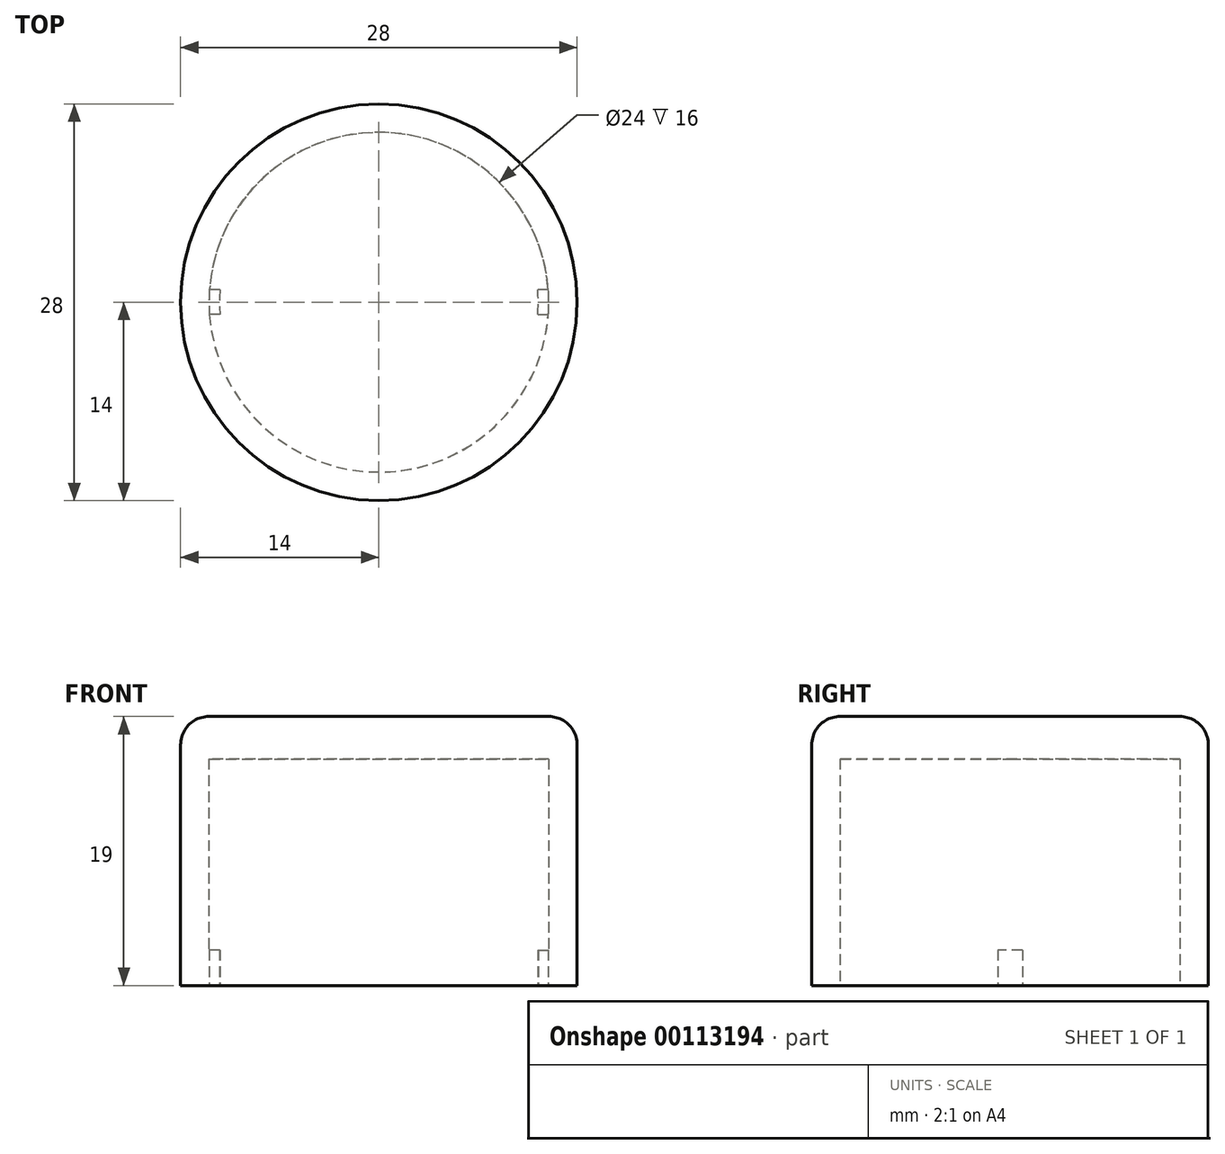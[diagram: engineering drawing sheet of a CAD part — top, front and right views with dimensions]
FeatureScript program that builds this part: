
annotation { "Feature Type Name" : "Feature", "Feature Type Description" : "" }
export const myFeature = defineFeature(function(context is Context, id is Id, definition is map)
    precondition{}
    {
        {
            var Q0;
            Q0=qCreatedBy(makeId("Top.planeOp"),FACE);
            var sketch = newSketch(context, id + "F0", { "sketchPlane" : qUnion([Q0])});
            skCircle(sketch, "E0", {"center": v(0, 0) * mm, "radius": 12 * mm});
            skCircle(sketch, "E1.0", {"center": v(0, 0) * mm, "radius": 14 * mm});
            skSolve(sketch);
        }
        {
            var Q0;
            Q0=makeQuery(id+"F0.imprint","IMPRINT",FACE,{"disambiguationData":[TD([[makeQuery(id+"F0.imprint","IMPRINT",EDGE,{"derivedFrom":sQuery(id+"F0.wireOp",EDGE,"E0")}),-1.0]])]});
            extrude(context, id + "F1", {"entities" : qUnion([Q0]), "depth" : 16 * mm});
        }
        {
            var Q0;
            Q0=qCreatedBy(makeId("Top.planeOp"),FACE);
            var sketch = newSketch(context, id + "F2", { "sketchPlane" : qUnion([Q0])});
            skLineSegment(sketch, "E2", {"start": v(12, 0) * mm, "end": v(-12, 0) * mm, "construction": true});
            skArc(sketch, "E3.0", {"start": v(-11.97, 0.87) * mm, "mid": v(-12, 0) * mm, "end": v(-11.97, -0.87) * mm});
            skLineSegment(sketch, "E4", {"start": v(11.97, 0.88) * mm, "end": v(11.22, 0.88) * mm});
            skLineSegment(sketch, "E5", {"start": v(11.22, -0.88) * mm, "end": v(11.97, -0.88) * mm});
            skArc(sketch, "E6", {"start": v(-11.22, 0.87) * mm, "mid": v(-11.25, 0) * mm, "end": v(-11.22, -0.87) * mm});
            skLineSegment(sketch, "E7", {"start": v(-11.22, 0.88) * mm, "end": v(-11.97, 0.88) * mm});
            skLineSegment(sketch, "E8", {"start": v(-11.22, -0.88) * mm, "end": v(-11.97, -0.88) * mm});
            skLineSegment(sketch, "E9", {"start": v(11.6, 0.87) * mm, "end": v(11.6, -0.88) * mm, "construction": true});
            skPoint(sketch, "E10", {"position": v(11.6, 0) * mm});
            skArc(sketch, "E11.trimOffspring", {"start": v(11.97, -0.87) * mm, "mid": v(12, 0) * mm, "end": v(11.97, 0.87) * mm});
            skArc(sketch, "E12.trimOffspring", {"start": v(11.22, -0.87) * mm, "mid": v(11.25, 0) * mm, "end": v(11.22, 0.88) * mm});
            skSolve(sketch);
        }
        {
            var Q0;
            Q0=qSketchRegion(id+"F2",true);
            extrude(context, id + "F3", {"entities" : qUnion([Q0]), "operationType" : NewBodyOperationType.ADD, "depth" : 2.5 * mm});
        }
        {
            var Q0;
            Q0=makeQuery(id+"F1.opExtrude","CAP_FACE",FACE,{"disambiguationData":[OSD([sQuery(id+"F0.wireOp",EDGE,"E0"),sQuery(id+"F0.wireOp",EDGE,"E1.0")])],"isStart":false});
            var sketch = newSketch(context, id + "F4", { "sketchPlane" : qUnion([Q0])});
            skCircle(sketch, "E13.0", {"center": v(0, 0) * mm, "radius": 14 * mm});
            skSolve(sketch);
        }
        {
            var Q0;
            Q0 = qSketchRegion(id + "F4", true);
            extrude(context, id + "F5", {"entities" : qUnion([Q0]), "operationType" : NewBodyOperationType.ADD, "depth" : 3 * mm});
        }
        {
            var Q0;
            Q0=makeQuery(id+"F5.opExtrude","CAP_EDGE",EDGE,{"disambiguationData":[OSD([sQuery(id+"F4.wireOp",EDGE,"E13.0")])],"isStart":false});
            fillet(context, id + "F6", {"entities" : qUnion([Q0]), "radius" : 2 * mm, "tangentPropagation" : true, "allowEdgeOverflow" : false});
        }
    });
